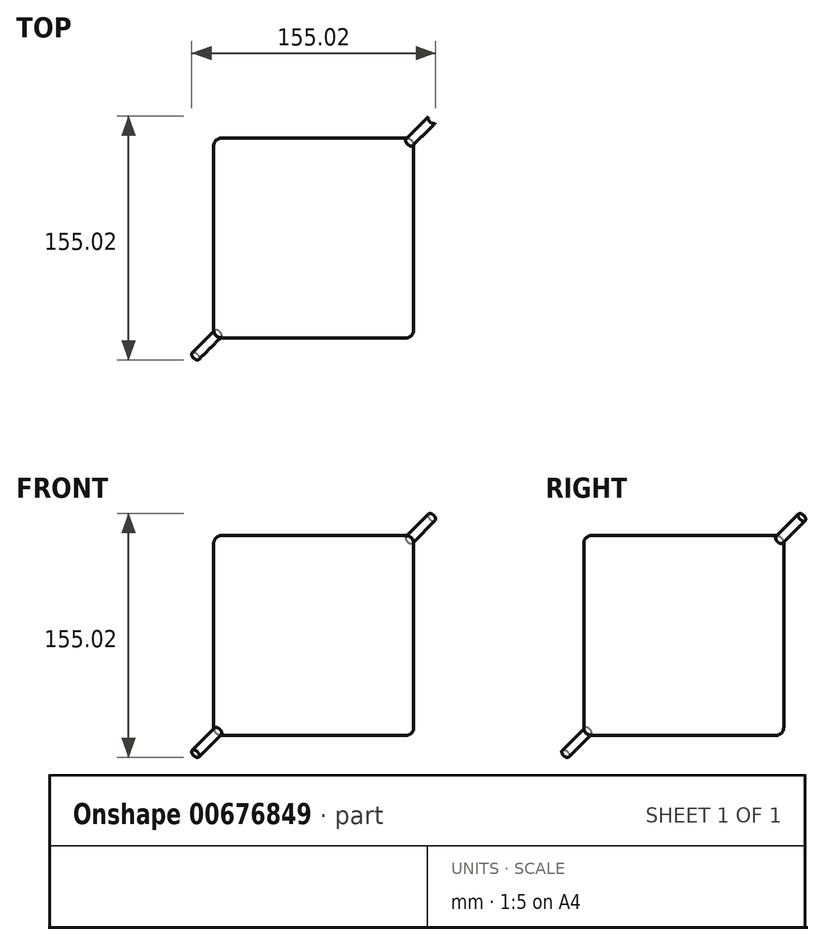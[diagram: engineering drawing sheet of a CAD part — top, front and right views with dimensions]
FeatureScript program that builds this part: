
annotation { "Feature Type Name" : "Feature", "Feature Type Description" : "" }
export const myFeature = defineFeature(function(context is Context, id is Id, definition is map)
    precondition{}
    {
        {
            var Q0;
            Q0=qCreatedBy(makeId("Top.planeOp"),FACE);
            var sketch = newSketch(context, id + "F0", { "sketchPlane" : qUnion([Q0])});
            skCircle(sketch, "E0.cCircle", {"center": v(0, 0) * mm, "radius": 63.5 * mm, "construction": true});
            skLineSegment(sketch, "E0.0", {"start": v(63.5, 63.5) * mm, "end": v(63.5, -63.5) * mm});
            skLineSegment(sketch, "E0.1", {"start": v(63.5, -63.5) * mm, "end": v(-63.5, -63.5) * mm});
            skLineSegment(sketch, "E0.2", {"start": v(-63.5, -63.5) * mm, "end": v(-63.5, 63.5) * mm});
            skLineSegment(sketch, "E0.3", {"start": v(-63.5, 63.5) * mm, "end": v(63.5, 63.5) * mm});
            skPoint(sketch, "E0.0.midPoint", {"position": v(63.5, 0) * mm});
            skSolve(sketch);
        }
        {
            var Q0;
            Q0=makeQuery(id+"F0.imprint","IMPRINT",FACE,{"disambiguationData":[TD([[makeQuery(id+"F0.imprint","IMPRINT",EDGE,{"derivedFrom":sQuery(id+"F0.wireOp",EDGE,"E0.0")}),-1.0]])]});
            extrude(context, id + "F1", {"entities" : qUnion([Q0]), "endBound" : BoundingType.SYMMETRIC, "depth" : 127 * mm, "offsetDistance" : 25 * mm});
        }
        {
            var Q0;
            Q0=makeQuery(id+"F1.opExtrude","CAP_VERTEX",VERTEX,{"disambiguationData":[OSD([sQuery(id+"F0.wireOp",EDGE,"E0.1"),sQuery(id+"F0.wireOp",EDGE,"E0.2")])],"isStart":true});
            var Q1;
            Q1=makeQuery(id+"F1.opExtrude","CAP_VERTEX",VERTEX,{"disambiguationData":[OSD([sQuery(id+"F0.wireOp",EDGE,"E0.1"),sQuery(id+"F0.wireOp",EDGE,"E0.2")])],"isStart":false});
            var Q2;
            Q2=makeQuery(id+"F1.opExtrude","CAP_VERTEX",VERTEX,{"disambiguationData":[OSD([sQuery(id+"F0.wireOp",EDGE,"E0.0"),sQuery(id+"F0.wireOp",EDGE,"E0.3")])],"isStart":false});
            cPlane(context, id + "F2", {"entities" : qUnion([Q0, Q1, Q2]), "cplaneType" : CPlaneType.THREE_POINT, "offset" : 25 * mm, "width" : 150 * mm, "height" : 150 * mm});
        }
        {
            var Q0;
            Q0=qCreatedBy(id+"F2.planeOp",FACE);
            var sketch = newSketch(context, id + "F3", { "sketchPlane" : qUnion([Q0])});
            skPoint(sketch, "E1.0", {"position": v(-89.8, -63.5) * mm});
            skPoint(sketch, "E2.0", {"position": v(89.8, 63.5) * mm});
            skLineSegment(sketch, "E3", {"start": v(106.14, 75.06) * mm, "end": v(104.41, 77.5) * mm});
            skLineSegment(sketch, "E4", {"start": v(104.41, 77.5) * mm, "end": v(-107.88, -72.6) * mm});
            skLineSegment(sketch, "E5", {"start": v(-107.88, -72.6) * mm, "end": v(-106.14, -75.06) * mm});
            skLineSegment(sketch, "E6", {"start": v(-106.14, -75.06) * mm, "end": v(106.14, 75.06) * mm});
            skSolve(sketch);
        }
        {
            var Q0;
            Q0=makeQuery(id+"F1.opExtrude","CAP_FACE",FACE,{"disambiguationData":[OSD([sQuery(id+"F0.wireOp",EDGE,"E0.0"),sQuery(id+"F0.wireOp",EDGE,"E0.1"),sQuery(id+"F0.wireOp",EDGE,"E0.2"),sQuery(id+"F0.wireOp",EDGE,"E0.3")])],"isStart":false});
            var Q1;
            Q1=makeQuery(id+"F1.opExtrude","SWEPT_FACE",FACE,{"disambiguationData":[OSD([sQuery(id+"F0.wireOp",EDGE,"E0.1")])]});
            var Q2;
            Q2=makeQuery(id+"F1.opExtrude","SWEPT_FACE",FACE,{"disambiguationData":[OSD([sQuery(id+"F0.wireOp",EDGE,"E0.0")])]});
            var Q3;
            Q3=makeQuery(id+"F1.opExtrude","CAP_FACE",FACE,{"disambiguationData":[OSD([sQuery(id+"F0.wireOp",EDGE,"E0.0"),sQuery(id+"F0.wireOp",EDGE,"E0.1"),sQuery(id+"F0.wireOp",EDGE,"E0.2"),sQuery(id+"F0.wireOp",EDGE,"E0.3")])],"isStart":true});
            var Q4;
            Q4=makeQuery(id+"F1.opExtrude","SWEPT_FACE",FACE,{"disambiguationData":[OSD([sQuery(id+"F0.wireOp",EDGE,"E0.3")])]});
            var Q5;
            Q5=makeQuery(id+"F1.opExtrude","SWEPT_FACE",FACE,{"disambiguationData":[OSD([sQuery(id+"F0.wireOp",EDGE,"E0.2")])]});
            fillet(context, id + "F4", {"entities" : qUnion([Q0, Q1, Q2, Q3, Q4, Q5]), "radius" : 5 * mm, "tangentPropagation" : true, "allowEdgeOverflow" : false});
        }
        {
            var Q0;
            Q0=makeQuery(id+"F3.imprint","IMPRINT",FACE,{"disambiguationData":[TD([[makeQuery(id+"F3.imprint","IMPRINT",EDGE,{"derivedFrom":sQuery(id+"F3.wireOp",EDGE,"E3")}),1.0]])]});
            var Q1;
            Q1=sQuery(id+"F3.wireOp",EDGE,"E6");
            revolve(context, id + "F5", {"operationType" : NewBodyOperationType.ADD, "surfaceOperationType" : NewSurfaceOperationType.NEW, "entities" : qUnion([Q0]), "axis" : qUnion([Q1]), "revolveType" : RevolveType.FULL});
        }
    });
